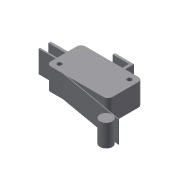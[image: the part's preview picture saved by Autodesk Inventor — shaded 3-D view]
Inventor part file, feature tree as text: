
AUTODESK INVENTOR PART (.ipt)
format: ipt  version: 2019.4 (Build 234330000, 330)  size: 129,024 bytes
history: native  units: mm
features: extrude x2, sketch x2
ambient origin geometry x8: Origin, YZ Plane, XZ Plane, XY Plane, X Axis, Y Axis, Z Axis, Center Point
bodies: Solid1 (feature_tree)
feature tree (4):
  extrude  "Extrusion1"  Depth=15.7mm
  extrude  "Extrusion2"  Depth=10.0mm TaperAngle=0.0deg
  sketch  "Sketch1"  dims[d0=27.85mm d1=15.7mm]
  sketch  "Sketch2"  dims[d2=2.0mm d3=10.0mm d4=0.0mm d5=29.670597mm d6=10.0mm d7=2.0mm d8=2.0mm d9=3.0mm d10=3.0mm d11=3.0mm d12=3.0mm d13=10.0mm d14=0.0mm]
